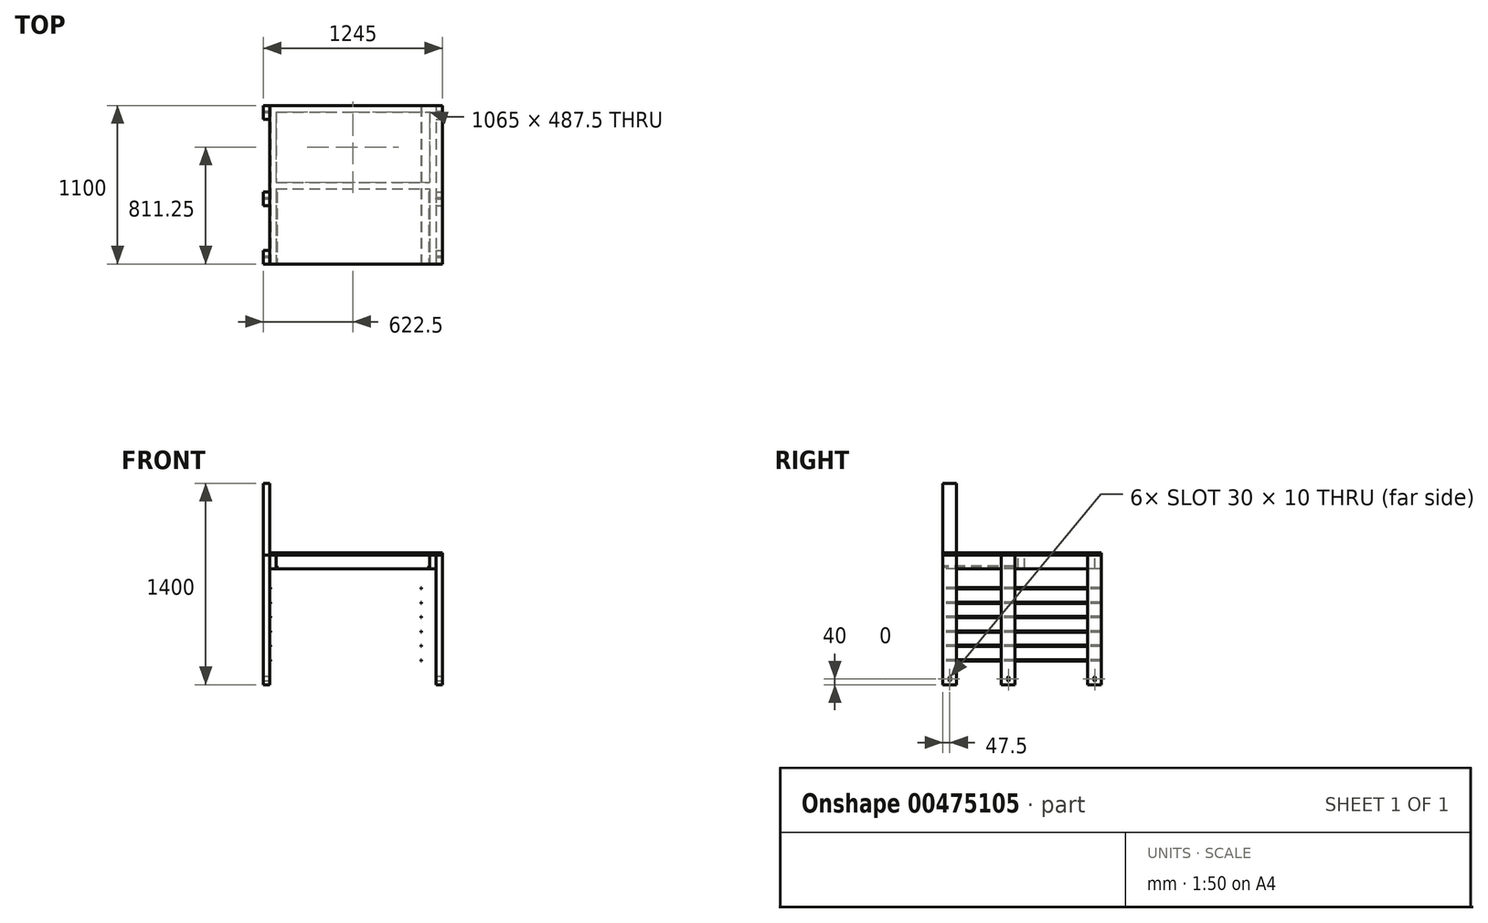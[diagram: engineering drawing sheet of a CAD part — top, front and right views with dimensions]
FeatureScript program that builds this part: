
annotation { "Feature Type Name" : "Feature", "Feature Type Description" : "" }
export const myFeature = defineFeature(function(context is Context, id is Id, definition is map)
    precondition{}
    {
        {
            var Q0;
            Q0=qCreatedBy(makeId("Top.planeOp"),FACE);
            var sketch = newSketch(context, id + "F0", { "sketchPlane" : qUnion([Q0])});
            skLineSegment(sketch, "E0.bottom", {"start": v(-600, 550) * mm, "end": v(600, 550) * mm});
            skLineSegment(sketch, "E0.top", {"start": v(-600, -550) * mm, "end": v(600, -550) * mm});
            skLineSegment(sketch, "E0.left", {"start": v(-600, 550) * mm, "end": v(-600, -550) * mm});
            skLineSegment(sketch, "E0.right", {"start": v(600, 550) * mm, "end": v(600, -550) * mm});
            skSolve(sketch);
        }
        {
            var Q0;
            Q0=qCreatedBy(makeId("Top.planeOp"),FACE);
            var sketch = newSketch(context, id + "F1", { "sketchPlane" : qUnion([Q0])});
            skLineSegment(sketch, "E1.bottom", {"start": v(-600, 550) * mm, "end": v(600, 550) * mm, "construction": true});
            skLineSegment(sketch, "E1.top", {"start": v(-600, -550) * mm, "end": v(600, -550) * mm, "construction": true});
            skLineSegment(sketch, "E1.left", {"start": v(-600, 550) * mm, "end": v(-600, -550) * mm, "construction": true});
            skLineSegment(sketch, "E1.right", {"start": v(600, 550) * mm, "end": v(600, -550) * mm, "construction": true});
            skLineSegment(sketch, "E2.bottom", {"start": v(-600, 550) * mm, "end": v(-555, 550) * mm});
            skLineSegment(sketch, "E2.top", {"start": v(-600, -550) * mm, "end": v(-555, -550) * mm});
            skLineSegment(sketch, "E2.left", {"start": v(-600, 550) * mm, "end": v(-600, -550) * mm});
            skLineSegment(sketch, "E2.right", {"start": v(-555, 550) * mm, "end": v(-555, -550) * mm});
            skLineSegment(sketch, "E3.bottom", {"start": v(510, 550) * mm, "end": v(555, 550) * mm});
            skLineSegment(sketch, "E3.top", {"start": v(510, -550) * mm, "end": v(555, -550) * mm});
            skLineSegment(sketch, "E3.left", {"start": v(510, 550) * mm, "end": v(510, -550) * mm});
            skLineSegment(sketch, "E3.right", {"start": v(555, 550) * mm, "end": v(555, -550) * mm});
            skLineSegment(sketch, "E4.bottom", {"start": v(-555, 17.5) * mm, "end": v(510, 17.5) * mm});
            skLineSegment(sketch, "E4.top", {"start": v(-555, -27.5) * mm, "end": v(510, -27.5) * mm});
            skLineSegment(sketch, "E4.left", {"start": v(-555, 17.5) * mm, "end": v(-555, -27.5) * mm});
            skLineSegment(sketch, "E4.right", {"start": v(510, 17.5) * mm, "end": v(510, -27.5) * mm});
            skLineSegment(sketch, "E5.bottom", {"start": v(-555, 550) * mm, "end": v(510, 550) * mm});
            skLineSegment(sketch, "E5.top", {"start": v(-555, 505) * mm, "end": v(510, 505) * mm});
            skLineSegment(sketch, "E5.left", {"start": v(-555, 550) * mm, "end": v(-555, 505) * mm});
            skLineSegment(sketch, "E5.right", {"start": v(510, 550) * mm, "end": v(510, 505) * mm});
            skSolve(sketch);
        }
        {
            var Q0;
            Q0 = qSketchRegion(id + "F0", true);
            extrude(context, id + "F2", {"entities" : qUnion([Q0]), "depth" : 18 * mm});
        }
        {
            var Q0;
            Q0=qCreatedBy(makeId("Top.planeOp"),FACE);
            var sketch = newSketch(context, id + "F3", { "sketchPlane" : qUnion([Q0])});
            skLineSegment(sketch, "E6.bottom", {"start": v(-600, 550) * mm, "end": v(600, 550) * mm, "construction": true});
            skLineSegment(sketch, "E6.top", {"start": v(-600, -550) * mm, "end": v(600, -550) * mm, "construction": true});
            skLineSegment(sketch, "E6.left", {"start": v(-600, 550) * mm, "end": v(-600, -550) * mm, "construction": true});
            skLineSegment(sketch, "E6.right", {"start": v(600, 550) * mm, "end": v(600, -550) * mm, "construction": true});
            skLineSegment(sketch, "E7.bottom", {"start": v(-600, 550) * mm, "end": v(-645, 550) * mm, "construction": true});
            skLineSegment(sketch, "E7.top", {"start": v(-600, -550) * mm, "end": v(-645, -550) * mm, "construction": true});
            skLineSegment(sketch, "E7.right", {"start": v(-645, 550) * mm, "end": v(-645, -550) * mm, "construction": true});
            skLineSegment(sketch, "E8", {"start": v(555, 550) * mm, "end": v(555, -550) * mm, "construction": true});
            skLineSegment(sketch, "E9", {"start": v(-645, -455) * mm, "end": v(600, -455) * mm, "construction": true});
            skLineSegment(sketch, "E10", {"start": v(-645, -145) * mm, "end": v(600, -145) * mm, "construction": true});
            skLineSegment(sketch, "E11", {"start": v(-645, -50) * mm, "end": v(600, -50) * mm, "construction": true});
            skLineSegment(sketch, "E12", {"start": v(-645, 455) * mm, "end": v(600, 455) * mm, "construction": true});
            skLineSegment(sketch, "E13.bottom", {"start": v(-645, 550) * mm, "end": v(-600, 550) * mm});
            skLineSegment(sketch, "E13.top", {"start": v(-645, 455) * mm, "end": v(-600, 455) * mm});
            skLineSegment(sketch, "E13.left", {"start": v(-645, 550) * mm, "end": v(-645, 455) * mm});
            skLineSegment(sketch, "E13.right", {"start": v(-600, 550) * mm, "end": v(-600, 455) * mm});
            skLineSegment(sketch, "E14.bottom", {"start": v(-645, -50) * mm, "end": v(-600, -50) * mm});
            skLineSegment(sketch, "E14.top", {"start": v(-645, -145) * mm, "end": v(-600, -145) * mm});
            skLineSegment(sketch, "E14.left", {"start": v(-645, -50) * mm, "end": v(-645, -145) * mm});
            skLineSegment(sketch, "E14.right", {"start": v(-600, -50) * mm, "end": v(-600, -145) * mm});
            skLineSegment(sketch, "E15.bottom", {"start": v(-645, -455) * mm, "end": v(-600, -455) * mm});
            skLineSegment(sketch, "E15.top", {"start": v(-645, -550) * mm, "end": v(-600, -550) * mm});
            skLineSegment(sketch, "E15.left", {"start": v(-645, -455) * mm, "end": v(-645, -550) * mm});
            skLineSegment(sketch, "E15.right", {"start": v(-600, -455) * mm, "end": v(-600, -550) * mm});
            skLineSegment(sketch, "E16.bottom", {"start": v(555, -455) * mm, "end": v(600, -455) * mm});
            skLineSegment(sketch, "E16.top", {"start": v(555, -550) * mm, "end": v(600, -550) * mm});
            skLineSegment(sketch, "E16.left", {"start": v(555, -455) * mm, "end": v(555, -550) * mm});
            skLineSegment(sketch, "E16.right", {"start": v(600, -455) * mm, "end": v(600, -550) * mm});
            skLineSegment(sketch, "E17.bottom", {"start": v(555, -50) * mm, "end": v(600, -50) * mm});
            skLineSegment(sketch, "E17.top", {"start": v(555, -145) * mm, "end": v(600, -145) * mm});
            skLineSegment(sketch, "E17.left", {"start": v(555, -50) * mm, "end": v(555, -145) * mm});
            skLineSegment(sketch, "E17.right", {"start": v(600, -50) * mm, "end": v(600, -145) * mm});
            skLineSegment(sketch, "E18.bottom", {"start": v(555, 550) * mm, "end": v(600, 550) * mm});
            skLineSegment(sketch, "E18.top", {"start": v(555, 455) * mm, "end": v(600, 455) * mm});
            skLineSegment(sketch, "E18.left", {"start": v(555, 550) * mm, "end": v(555, 455) * mm});
            skLineSegment(sketch, "E18.right", {"start": v(600, 550) * mm, "end": v(600, 455) * mm});
            skSolve(sketch);
        }
        {
            var Q0;
            Q0 = qSketchRegion(id + "F3", true);
            extrude(context, id + "F4", {"entities" : qUnion([Q0]), "oppositeDirection" : true, "depth" : 900 * mm});
        }
        {
            var Q0;
            Q0=makeQuery(id+"F4.opExtrude","CAP_FACE",FACE,{"disambiguationData":[OSD([sQuery(id+"F3.wireOp",EDGE,"E15.bottom"),sQuery(id+"F3.wireOp",EDGE,"E15.top"),sQuery(id+"F3.wireOp",EDGE,"E15.left"),sQuery(id+"F3.wireOp",EDGE,"E15.right")])],"isStart":true});
            extrude(context, id + "F5", {"entities" : qUnion([Q0]), "depth" : 500 * mm, "offsetDistance" : 25 * mm});
        }
        {
            var Q0;
            Q0=makeQuery(id+"F1.imprint","IMPRINT",FACE,{"disambiguationData":[TD([[makeQuery(id+"F1.imprint","IMPRINT",EDGE,{"derivedFrom":sQuery(id+"F1.wireOp",EDGE,"E2.bottom")}),-1.0]])]});
            var Q1;
            Q1=makeQuery(id+"F1.imprint","IMPRINT",FACE,{"disambiguationData":[TD([[makeQuery(id+"F1.imprint","IMPRINT",EDGE,{"derivedFrom":sQuery(id+"F1.wireOp",EDGE,"E5.bottom")}),-1.0]])]});
            var Q2;
            Q2=makeQuery(id+"F1.imprint","IMPRINT",FACE,{"disambiguationData":[TD([[makeQuery(id+"F1.imprint","IMPRINT",EDGE,{"derivedFrom":sQuery(id+"F1.wireOp",EDGE,"E4.bottom")}),-1.0]])]});
            var Q3;
            Q3=makeQuery(id+"F1.imprint","IMPRINT",FACE,{"disambiguationData":[TD([[makeQuery(id+"F1.imprint","IMPRINT",EDGE,{"derivedFrom":sQuery(id+"F1.wireOp",EDGE,"E3.bottom")}),-1.0]])]});
            extrude(context, id + "F6", {"entities" : qUnion([Q0, Q1, Q2, Q3]), "oppositeDirection" : true, "depth" : 95 * mm});
        }
        {
            var Q0;
            Q0=makeQuery(id+"F4.opExtrude","SWEPT_FACE",FACE,{"disambiguationData":[OSD([sQuery(id+"F3.wireOp",EDGE,"E15.left")])]});
            var sketch = newSketch(context, id + "F7", { "sketchPlane" : qUnion([Q0])});
            skLineSegment(sketch, "E19", {"start": v(502.5, -900) * mm, "end": v(502.5, -638.65) * mm, "construction": true});
            skLineSegment(sketch, "E20", {"start": v(455, -870) * mm, "end": v(550, -870) * mm});
            skLineSegment(sketch, "E21", {"start": v(455, -850) * mm, "end": v(550, -850) * mm});
            skLineSegment(sketch, "E22.bottom", {"start": v(497.5, -850) * mm, "end": v(507.5, -850) * mm});
            skLineSegment(sketch, "E22.top", {"start": v(497.5, -870) * mm, "end": v(507.5, -870) * mm});
            skLineSegment(sketch, "E22.left", {"start": v(497.5, -850) * mm, "end": v(497.5, -870) * mm});
            skLineSegment(sketch, "E22.right", {"start": v(507.5, -850) * mm, "end": v(507.5, -870) * mm});
            skCircle(sketch, "E23", {"center": v(502.5, -850) * mm, "radius": 5 * mm});
            skCircle(sketch, "E24", {"center": v(502.5, -870) * mm, "radius": 5 * mm});
            skLineSegment(sketch, "E25", {"start": v(470.22, -870) * mm, "end": v(-588.53, -870) * mm, "construction": true});
            skLineSegment(sketch, "E26", {"start": v(475.78, -850) * mm, "end": v(-587.86, -850) * mm, "construction": true});
            skLineSegment(sketch, "E27", {"start": v(95, -906.95) * mm, "end": v(95, -740.1) * mm, "construction": true});
            skLineSegment(sketch, "E28", {"start": v(-505, -913.55) * mm, "end": v(-505, -742.53) * mm, "construction": true});
            skLineSegment(sketch, "E29.bottom", {"start": v(90, -850) * mm, "end": v(100, -850) * mm});
            skLineSegment(sketch, "E29.top", {"start": v(90, -870) * mm, "end": v(100, -870) * mm});
            skLineSegment(sketch, "E29.left", {"start": v(90, -850) * mm, "end": v(90, -870) * mm});
            skLineSegment(sketch, "E29.right", {"start": v(100, -850) * mm, "end": v(100, -870) * mm});
            skLineSegment(sketch, "E30.bottom", {"start": v(-510, -850) * mm, "end": v(-500, -850) * mm});
            skLineSegment(sketch, "E30.top", {"start": v(-510, -870) * mm, "end": v(-500, -870) * mm});
            skLineSegment(sketch, "E30.left", {"start": v(-510, -850) * mm, "end": v(-510, -870) * mm});
            skLineSegment(sketch, "E30.right", {"start": v(-500, -850) * mm, "end": v(-500, -870) * mm});
            skCircle(sketch, "E31", {"center": v(-505, -850) * mm, "radius": 5 * mm});
            skCircle(sketch, "E32", {"center": v(-505, -870) * mm, "radius": 5 * mm});
            skCircle(sketch, "E33", {"center": v(95, -870) * mm, "radius": 5 * mm});
            skCircle(sketch, "E34", {"center": v(95, -850) * mm, "radius": 5 * mm});
            skSolve(sketch);
        }
        {
            var Q0;
            Q0 = qSketchRegion(id + "F7", true);
            extrude(context, id + "F8", {"entities" : qUnion([Q0]), "operationType" : NewBodyOperationType.REMOVE, "oppositeDirection" : true, "depth" : 2000 * mm});
        }
        {
            var Q0;
            Q0=makeQuery(id+"F6.opExtrude","SWEPT_FACE",FACE,{"disambiguationData":[OSD([sQuery(id+"F1.wireOp",EDGE,"E2.top")])]});
            var sketch = newSketch(context, id + "F9", { "sketchPlane" : qUnion([Q0])});
            skLineSegment(sketch, "E35.bottom", {"start": v(-555, -85) * mm, "end": v(-550, -85) * mm});
            skLineSegment(sketch, "E35.top", {"start": v(-555, -75) * mm, "end": v(-550, -75) * mm});
            skLineSegment(sketch, "E35.left", {"start": v(-555, -85) * mm, "end": v(-555, -75) * mm});
            skLineSegment(sketch, "E35.right", {"start": v(-550, -85) * mm, "end": v(-550, -75) * mm});
            skSolve(sketch);
        }
        {
            var Q0;
            Q0 = qSketchRegion(id + "F9", true);
            extrude(context, id + "F10", {"entities" : qUnion([Q0]), "oppositeDirection" : true, "depth" : 500 * mm});
        }
        {
            var Q0;
            Q0=makeQuery(id+"F6.opExtrude","SWEPT_FACE",FACE,{"disambiguationData":[OSD([sQuery(id+"F1.wireOp",EDGE,"E3.top")])]});
            var sketch = newSketch(context, id + "F11", { "sketchPlane" : qUnion([Q0])});
            skLineSegment(sketch, "E36.bottom", {"start": v(510, -75) * mm, "end": v(505, -75) * mm});
            skLineSegment(sketch, "E36.top", {"start": v(510, -85) * mm, "end": v(505, -85) * mm});
            skLineSegment(sketch, "E36.left", {"start": v(510, -75) * mm, "end": v(510, -85) * mm});
            skLineSegment(sketch, "E36.right", {"start": v(505, -75) * mm, "end": v(505, -85) * mm});
            skSolve(sketch);
        }
        {
            var Q0;
            Q0 = qSketchRegion(id + "F11", true);
            extrude(context, id + "F12", {"entities" : qUnion([Q0]), "oppositeDirection" : true, "depth" : 500 * mm});
        }
        {
            var Q0;
            Q0=makeQuery(id+"F4.opExtrude","SWEPT_FACE",FACE,{"disambiguationData":[OSD([sQuery(id+"F3.wireOp",EDGE,"E15.top")])]});
            var sketch = newSketch(context, id + "F13", { "sketchPlane" : qUnion([Q0])});
            skLineSegment(sketch, "E37.bottom", {"start": v(-600, -225) * mm, "end": v(-595, -225) * mm});
            skLineSegment(sketch, "E37.top", {"start": v(-600, -235) * mm, "end": v(-595, -235) * mm});
            skLineSegment(sketch, "E37.left", {"start": v(-600, -225) * mm, "end": v(-600, -235) * mm});
            skLineSegment(sketch, "E37.right", {"start": v(-595, -225) * mm, "end": v(-595, -235) * mm});
            skLineSegment(sketch, "E38.bottom", {"start": v(-600, -325) * mm, "end": v(-595, -325) * mm});
            skLineSegment(sketch, "E38.top", {"start": v(-600, -335) * mm, "end": v(-595, -335) * mm});
            skLineSegment(sketch, "E38.left", {"start": v(-600, -325) * mm, "end": v(-600, -335) * mm});
            skLineSegment(sketch, "E38.right", {"start": v(-595, -325) * mm, "end": v(-595, -335) * mm});
            skLineSegment(sketch, "E39.bottom", {"start": v(-600, -425) * mm, "end": v(-595, -425) * mm});
            skLineSegment(sketch, "E39.top", {"start": v(-600, -435) * mm, "end": v(-595, -435) * mm});
            skLineSegment(sketch, "E39.left", {"start": v(-600, -425) * mm, "end": v(-600, -435) * mm});
            skLineSegment(sketch, "E39.right", {"start": v(-595, -425) * mm, "end": v(-595, -435) * mm});
            skLineSegment(sketch, "E40.bottom", {"start": v(-600, -525) * mm, "end": v(-595, -525) * mm});
            skLineSegment(sketch, "E40.top", {"start": v(-600, -535) * mm, "end": v(-595, -535) * mm});
            skLineSegment(sketch, "E40.left", {"start": v(-600, -525) * mm, "end": v(-600, -535) * mm});
            skLineSegment(sketch, "E40.right", {"start": v(-595, -525) * mm, "end": v(-595, -535) * mm});
            skLineSegment(sketch, "E41.bottom", {"start": v(-600, -625) * mm, "end": v(-595, -625) * mm});
            skLineSegment(sketch, "E41.top", {"start": v(-600, -635) * mm, "end": v(-595, -635) * mm});
            skLineSegment(sketch, "E41.left", {"start": v(-600, -625) * mm, "end": v(-600, -635) * mm});
            skLineSegment(sketch, "E41.right", {"start": v(-595, -625) * mm, "end": v(-595, -635) * mm});
            skLineSegment(sketch, "E42.bottom", {"start": v(-600, -725) * mm, "end": v(-595, -725) * mm});
            skLineSegment(sketch, "E42.top", {"start": v(-600, -735) * mm, "end": v(-595, -735) * mm});
            skLineSegment(sketch, "E42.left", {"start": v(-600, -725) * mm, "end": v(-600, -735) * mm});
            skLineSegment(sketch, "E42.right", {"start": v(-595, -725) * mm, "end": v(-595, -735) * mm});
            skLineSegment(sketch, "E43.bottom", {"start": v(450, -225) * mm, "end": v(455, -225) * mm});
            skLineSegment(sketch, "E43.top", {"start": v(450, -235) * mm, "end": v(455, -235) * mm});
            skLineSegment(sketch, "E43.left", {"start": v(450, -225) * mm, "end": v(450, -235) * mm});
            skLineSegment(sketch, "E43.right", {"start": v(455, -225) * mm, "end": v(455, -235) * mm});
            skLineSegment(sketch, "E44.bottom", {"start": v(450, -325) * mm, "end": v(455, -325) * mm});
            skLineSegment(sketch, "E44.top", {"start": v(450, -335) * mm, "end": v(455, -335) * mm});
            skLineSegment(sketch, "E44.left", {"start": v(450, -325) * mm, "end": v(450, -335) * mm});
            skLineSegment(sketch, "E44.right", {"start": v(455, -325) * mm, "end": v(455, -335) * mm});
            skLineSegment(sketch, "E45.bottom", {"start": v(450, -425) * mm, "end": v(455, -425) * mm});
            skLineSegment(sketch, "E45.top", {"start": v(450, -435) * mm, "end": v(455, -435) * mm});
            skLineSegment(sketch, "E45.left", {"start": v(450, -425) * mm, "end": v(450, -435) * mm});
            skLineSegment(sketch, "E45.right", {"start": v(455, -425) * mm, "end": v(455, -435) * mm});
            skLineSegment(sketch, "E46.bottom", {"start": v(450, -525) * mm, "end": v(455, -525) * mm});
            skLineSegment(sketch, "E46.top", {"start": v(450, -535) * mm, "end": v(455, -535) * mm});
            skLineSegment(sketch, "E46.left", {"start": v(450, -525) * mm, "end": v(450, -535) * mm});
            skLineSegment(sketch, "E46.right", {"start": v(455, -525) * mm, "end": v(455, -535) * mm});
            skLineSegment(sketch, "E47.bottom", {"start": v(450, -625) * mm, "end": v(455, -625) * mm});
            skLineSegment(sketch, "E47.top", {"start": v(450, -635) * mm, "end": v(455, -635) * mm});
            skLineSegment(sketch, "E47.left", {"start": v(450, -625) * mm, "end": v(450, -635) * mm});
            skLineSegment(sketch, "E47.right", {"start": v(455, -625) * mm, "end": v(455, -635) * mm});
            skLineSegment(sketch, "E48.bottom", {"start": v(450, -725) * mm, "end": v(455, -725) * mm});
            skLineSegment(sketch, "E48.top", {"start": v(450, -735) * mm, "end": v(455, -735) * mm});
            skLineSegment(sketch, "E48.left", {"start": v(450, -725) * mm, "end": v(450, -735) * mm});
            skLineSegment(sketch, "E48.right", {"start": v(455, -725) * mm, "end": v(455, -735) * mm});
            skLineSegment(sketch, "E49", {"start": v(-597.5, -225) * mm, "end": v(557.17, -225) * mm, "construction": true});
            skPoint(sketch, "E49.endSnap0", {"position": v(-597.5, -225) * mm});
            skLineSegment(sketch, "E50", {"start": v(455, -225) * mm, "end": v(455, -1033.35) * mm, "construction": true});
            skSolve(sketch);
        }
        {
            var Q0;
            Q0 = qSketchRegion(id + "F13", true);
            extrude(context, id + "F14", {"entities" : qUnion([Q0]), "oppositeDirection" : true, "depth" : 1100 * mm});
        }
    });
